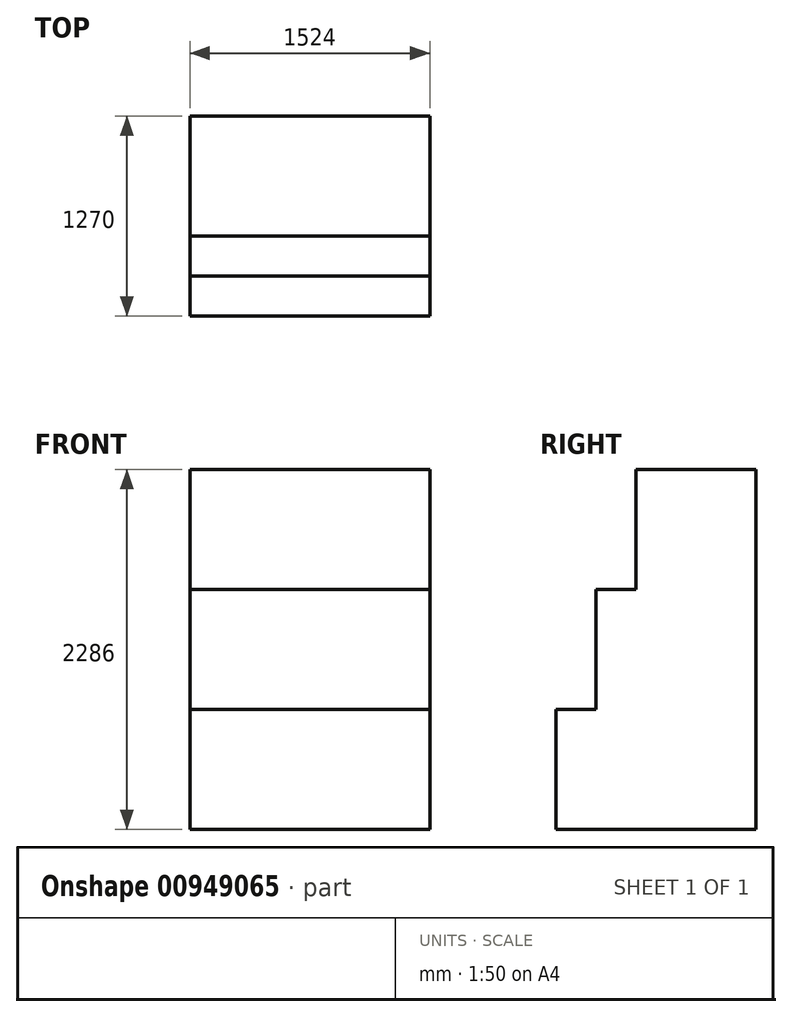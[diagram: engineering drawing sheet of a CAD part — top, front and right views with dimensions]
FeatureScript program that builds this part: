
annotation { "Feature Type Name" : "Feature", "Feature Type Description" : "" }
export const myFeature = defineFeature(function(context is Context, id is Id, definition is map)
    precondition{}
    {
        {
            var Q0;
            Q0=qCreatedBy(makeId("Right.planeOp"),FACE);
            var sketch = newSketch(context, id + "F0", { "sketchPlane" : qUnion([Q0])});
            skLineSegment(sketch, "E0", {"start": v(0, 0) * mm, "end": v(1270, 0) * mm});
            skLineSegment(sketch, "E1", {"start": v(1270, 0) * mm, "end": v(1270, 2286) * mm});
            skLineSegment(sketch, "E2", {"start": v(1270, 2286) * mm, "end": v(508, 2286) * mm});
            skLineSegment(sketch, "E3", {"start": v(508, 2286) * mm, "end": v(508, 1524) * mm});
            skLineSegment(sketch, "E4", {"start": v(508, 1524) * mm, "end": v(254, 1524) * mm});
            skLineSegment(sketch, "E5", {"start": v(254, 1524) * mm, "end": v(254, 762) * mm});
            skLineSegment(sketch, "E6", {"start": v(254, 762) * mm, "end": v(0, 762) * mm});
            skLineSegment(sketch, "E7", {"start": v(0, 762) * mm, "end": v(0, 0) * mm});
            skSolve(sketch);
        }
        {
            var Q0;
            Q0 = qSketchRegion(id + "F0", true);
            extrude(context, id + "F1", {"entities" : qUnion([Q0]), "depth" : 254 * mm, "offsetDistance" : 25.4 * mm});
        }
        {
            var Q0;
            Q0=makeQuery(id+"F1.opExtrude","CAP_FACE",FACE,{"disambiguationData":[OSD([sQuery(id+"F0.wireOp",EDGE,"E0"),sQuery(id+"F0.wireOp",EDGE,"E1"),sQuery(id+"F0.wireOp",EDGE,"E2"),sQuery(id+"F0.wireOp",EDGE,"E3"),sQuery(id+"F0.wireOp",EDGE,"E4"),sQuery(id+"F0.wireOp",EDGE,"E5"),sQuery(id+"F0.wireOp",EDGE,"E6"),sQuery(id+"F0.wireOp",EDGE,"E7")])],"isStart":false});
            extrude(context, id + "F2", {"entities" : qUnion([Q0]), "operationType" : NewBodyOperationType.ADD, "depth" : 1270 * mm, "offsetDistance" : 25.4 * mm});
        }
    });
